# Revit family: Wall_Union-Grohe-Euphoria_Cube-26634000
name_source: partatom
category: Plumbing Fixtures
units: mm (PartAtom-declared; Revit-internal decimal feet)

## family parameters
Cut with Voids When Loaded = No
Host = Face
OmniClass Number = 23.45.05.14.17
OmniClass Title = Showers
Part Type = Normal
Room Calculation Point = No
Round Connector Dimension = Use Diameter
Shared = Yes

## types (1)
- 26634000
    08565000 Non Return Valve = Yes
    Assembly Code = D2020
    CW Connection = No
    CWFU = 3
    Compliance Certifications = Energy Policy Act of 1992,• ASME A112.18.1/CSA B125.1,• CalGreen
• LOGO CEC
    Default Elevation = 0"
    Description = Euphoria Cube Wall Union
    Finish = Metal-Grohe-000-Starlight Chrome
    HW Connection = No
    HWFU = 3
    Height = 2 1/16"
    Installation Type = Wall Mounted
    Manufacturer = GROHE
    Material = Metal-Grohe-000-Starlight Chrome
    Model = 26634000
    Outlet Length = 1 3/16"
    Outlet Length Constraint = 1 3/16"
    Product Documentation Link = https://americanstandard.box.com
    Product Page URL = https://www.grohe.us
    Tempered Water Connection = Yes
    Tempered Water Connection Diameter = 1/2"
    URL = https://www.grohe.us
    Vent Connection = No
    WFU = 4
    Waste Connection = No
    Width = 2 5/8"
    cUPC Compliant = Yes

## geometry (parser evidence)
native form markers: Sweep x2
no freeform markers — native parametric forms only
